# Revit family: Skylight-Wasco-Ridge_System
name_source: partatom
category: Windows
revit_build: Autodesk Revit Architecture 2013 (Build: 20130531_2115(x64)
units: mm (PartAtom-declared; Revit-internal decimal feet)

## types (9) — shared parameters
Curb = Wood - Wasco - Douglas Firs
Curb Height = 0' - 3 1/32"
Curb Height C = 0' - 3 1/2"
Curb Width = 0' - 4"
Description = Skylight
EC H = 0' - 4 15/16"
Finish = Aluminum - Wasco - Aged Copper
Glazing 1 5_16 = Yes
Glazing Material = Glass - Wasco - Clear
Glazing Thickness = 0' - 1 5/16"
Manufacturer = Wasco
Product Documentation Link = http://www.wascoskylights.com
Product Name = Structural Ridge
Product Page URL = http://www.wascoskylights.com
Purlin = No
URL = http://www.wascoskylights.com

## per-type parameters (varying)
- Pinnacle 350 - 5/12: Angle=22.62°; C Masking Region Depth=0' - 6 23/32"; C Ridge Width=11' - 4 13/32"; Default Elevation=11' - 4 13/32"; Glazing Area=16.13 SF; Height=2' - 10 5/16"; Hypotenuse=6' - 2 1/32"; Length=22' - 0"; Masking Region Width=11' - 5 19/32"; Model=Pinnacle 350; P 12=No; P 5=Yes; P 7=No; Pinnacle 350=Yes; Pinnacle 600=No; Pinnacle 900=No; Pitch=5; Pitch Actual=5; Rafter Depth=0' - 5"; Ridge Height=2' - 4 15/32"; Ridge Height Offset=0' - 5 5/16"; Ridge Width=11' - 4 21/32"; Ridge Width Offset=0' - 2 7/32"; Rough Height=3' - 1 11/32"; Rough Width=11' - 4 21/32"; Sill Height Offset=0' - 0 17/32"; Sill Width Offset=0' - 0 5/16"; Width=11' - 0"; Width Actual=11' - 0"
- Pinnacle 600 - 5/12: Angle=22.62°; C Masking Region Depth=0' - 7 21/32"; C Ridge Width=20' - 6 11/32"; Default Elevation=20' - 6 11/32"; Glazing Area=54.57 SF; Height=4' - 11 17/32"; Hypotenuse=11' - 1 9/16"; Length=40' - 0"; Masking Region Width=20' - 7 1/2"; Model=Pinnacle 600; P 12=No; P 5=Yes; P 7=No; Pinnacle 350=No; Pinnacle 600=Yes; Pinnacle 900=No; Pitch=5; Pitch Actual=5; Rafter Depth=0' - 7 7/8"; Ridge Height=4' - 3 3/8"; Ridge Height Offset=0' - 7 5/8"; Ridge Width=20' - 6 19/32"; Ridge Width Offset=0' - 3 5/32"; Rough Height=5' - 2 9/16"; Rough Width=20' - 6 19/32"; Sill Height Offset=0' - 0 17/32"; Sill Width Offset=0' - 5 31/32"; Width=20' - 0"; Width Actual=20' - 0"
- Pinnacle 900 - 5/12: Angle=22.62°; C Masking Region Depth=0' - 8 11/16"; C Ridge Width=28' - 8 13/32"; Default Elevation=28' - 8 13/32"; Glazing Area=109.16 SF; Height=6' - 10 27/32"; Hypotenuse=15' - 7 5/8"; Length=56' - 0"; Masking Region Width=28' - 11 5/16"; Model=Pinnacle 900; P 12=No; P 5=Yes; P 7=No; Pinnacle 350=No; Pinnacle 600=No; Pinnacle 900=Yes; Pitch=5; Pitch Actual=5; Rafter Depth=0' - 10 3/4"; Ridge Height=6' - 0 5/32"; Ridge Height Offset=0' - 10 1/16"; Ridge Width=28' - 10 13/32"; Ridge Width Offset=0' - 4 3/16"; Rough Height=7' - 1 7/8"; Rough Width=28' - 10 13/32"; Sill Height Offset=0' - 0 5/8"; Sill Width Offset=0' - 5 3/4"; Width=28' - 0"; Width Actual=28' - 0"
- Pinnacle 350 - 7/12: Angle=30.26°; C Masking Region Depth=0' - 7 13/32"; C Ridge Width=10' - 5 13/16"; Default Elevation=10' - 5 13/16"; Glazing Area=14.6 SF; Height=3' - 6 9/32"; Hypotenuse=6' - 0 31/32"; Length=20' - 0"; Masking Region Width=10' - 6 29/32"; Model=Pinnacle 350; P 12=No; P 5=No; P 7=Yes; Pinnacle 350=Yes; Pinnacle 600=No; Pinnacle 900=No; Pitch=7; Pitch Actual=7; Rafter Depth=0' - 5"; Ridge Height=3' - 0 3/4"; Ridge Height Offset=0' - 4 31/32"; Ridge Width=10' - 6 1/16"; Ridge Width Offset=0' - 2 29/32"; Rough Height=3' - 9 5/16"; Rough Width=10' - 6 1/16"; Sill Height Offset=0' - 0 17/32"; Sill Width Offset=0' - 5 31/32"; Width=10' - 0"; Width Actual=10' - 0"
- Pinnacle 350 - 12/12: Angle=45.00°; C Masking Region Depth=0' - 8 5/8"; C Ridge Width=9' - 8 1/4"; Default Elevation=9' - 8 1/4"; Glazing Area=15.23 SF; Height=5' - 2 29/32"; Hypotenuse=6' - 10 3/8"; Length=18' - 0"; Masking Region Width=9' - 9 7/32"; Model=Pinnacle 350; P 12=Yes; P 5=No; P 7=No; Pinnacle 350=Yes; Pinnacle 600=No; Pinnacle 900=No; Pitch=12; Pitch Actual=12; Rafter Depth=0' - 5"; Ridge Height=4' - 10 1/4"; Ridge Height Offset=0' - 4 1/8"; Ridge Width=9' - 8 1/2"; Ridge Width Offset=0' - 4 1/8"; Rough Height=5' - 5 15/16"; Rough Width=9' - 8 1/2"; Sill Height Offset=0' - 0 17/32"; Sill Width Offset=0' - 5 31/32"; Width=9' - 0"; Width Actual=9' - 0"
- Pinnacle 600 - 7/12: Angle=30.26°; C Masking Region Depth=0' - 8 21/32"; C Ridge Width=19' - 8 5/16"; Default Elevation=19' - 8 5/16"; Glazing Area=53.64 SF; Height=6' - 4 21/32"; Hypotenuse=11' - 4 15/16"; Length=38' - 0"; Masking Region Width=19' - 9 13/32"; Model=Pinnacle 600; P 12=No; P 5=No; P 7=Yes; Pinnacle 350=No; Pinnacle 600=Yes; Pinnacle 900=No; Pitch=7; Pitch Actual=7; Rafter Depth=0' - 7 7/8"; Ridge Height=5' - 9"; Ridge Height Offset=0' - 7 1/8"; Ridge Width=19' - 8 9/16"; Ridge Width Offset=0' - 4 5/32"; Rough Height=6' - 7 11/16"; Rough Width=19' - 8 9/16"; Sill Height Offset=0' - 0 17/32"; Sill Width Offset=0' - 5 31/32"; Width=19' - 0"; Width Actual=19' - 0"
- Pinnacle 600 - 12/12: Angle=45.00°; C Masking Region Depth=0' - 10 13/32"; C Ridge Width=15' - 11 25/32"; Default Elevation=15' - 11 25/32"; Glazing Area=42.9 SF; Height=8' - 6 15/32"; Hypotenuse=11' - 3 25/32"; Length=30' - 0"; Masking Region Width=16' - 0 3/4"; Model=Pinnacle 600; P 12=Yes; P 5=No; P 7=No; Pinnacle 350=No; Pinnacle 600=Yes; Pinnacle 900=No; Pitch=12; Pitch Actual=12; Rafter Depth=0' - 7 7/8"; Ridge Height=8' - 0 1/32"; Ridge Height Offset=0' - 5 29/32"; Ridge Width=16' - 0 1/32"; Ridge Width Offset=0' - 5 29/32"; Rough Height=8' - 9 1/2"; Rough Width=16' - 0 1/32"; Sill Height Offset=0' - 0 17/32"; Sill Width Offset=0' - 5 31/32"; Width=15' - 0"; Width Actual=15' - 0"
- Pinnacle 900 - 7/12: Angle=30.26°; C Masking Region Depth=0' - 9 31/32"; C Ridge Width=27' - 4 29/32"; Default Elevation=27' - 4 29/32"; Glazing Area=106.4 SF; Height=8' - 10 1/2"; Hypotenuse=15' - 11 9/16"; Length=53' - 0"; Masking Region Width=27' - 7 25/32"; Model=Pinnacle 900; P 12=No; P 5=No; P 7=Yes; Pinnacle 350=No; Pinnacle 600=No; Pinnacle 900=Yes; Pitch=7; Pitch Actual=7; Rafter Depth=0' - 10 3/4"; Ridge Height=8' - 0 17/32"; Ridge Height Offset=0' - 9 11/32"; Ridge Width=27' - 6 29/32"; Ridge Width Offset=0' - 5 15/32"; Rough Height=9' - 1 17/32"; Rough Width=27' - 6 29/32"; Sill Height Offset=0' - 0 5/8"; Sill Width Offset=0' - 5 3/4"; Width=26' - 6"; Width Actual=26' - 6"
- Pinnacle 900 - 12/12: Angle=45.00°; C Masking Region Depth=1' - 0 1/32"; C Ridge Width=23' - 3 3/32"; Default Elevation=23' - 3 3/32"; Glazing Area=93.5 SF; Height=12' - 4 11/16"; Hypotenuse=16' - 6 3/4"; Length=44' - 0"; Masking Region Width=23' - 5 25/32"; Model=Pinnacle 900; P 12=Yes; P 5=No; P 7=No; Pinnacle 350=No; Pinnacle 600=No; Pinnacle 900=Yes; Pitch=12; Pitch Actual=12; Rafter Depth=0' - 10 3/4"; Ridge Height=11' - 8 17/32"; Ridge Height Offset=0' - 7 17/32"; Ridge Width=23' - 5 3/32"; Ridge Width Offset=0' - 7 17/32"; Rough Height=12' - 7 23/32"; Rough Width=23' - 5 3/32"; Sill Height Offset=0' - 0 5/8"; Sill Width Offset=0' - 5 3/4"; Width=22' - 0"; Width Actual=22' - 0"

## geometry (parser evidence)
native form markers: Blend x22, Sweep x10
no freeform markers — native parametric forms only
